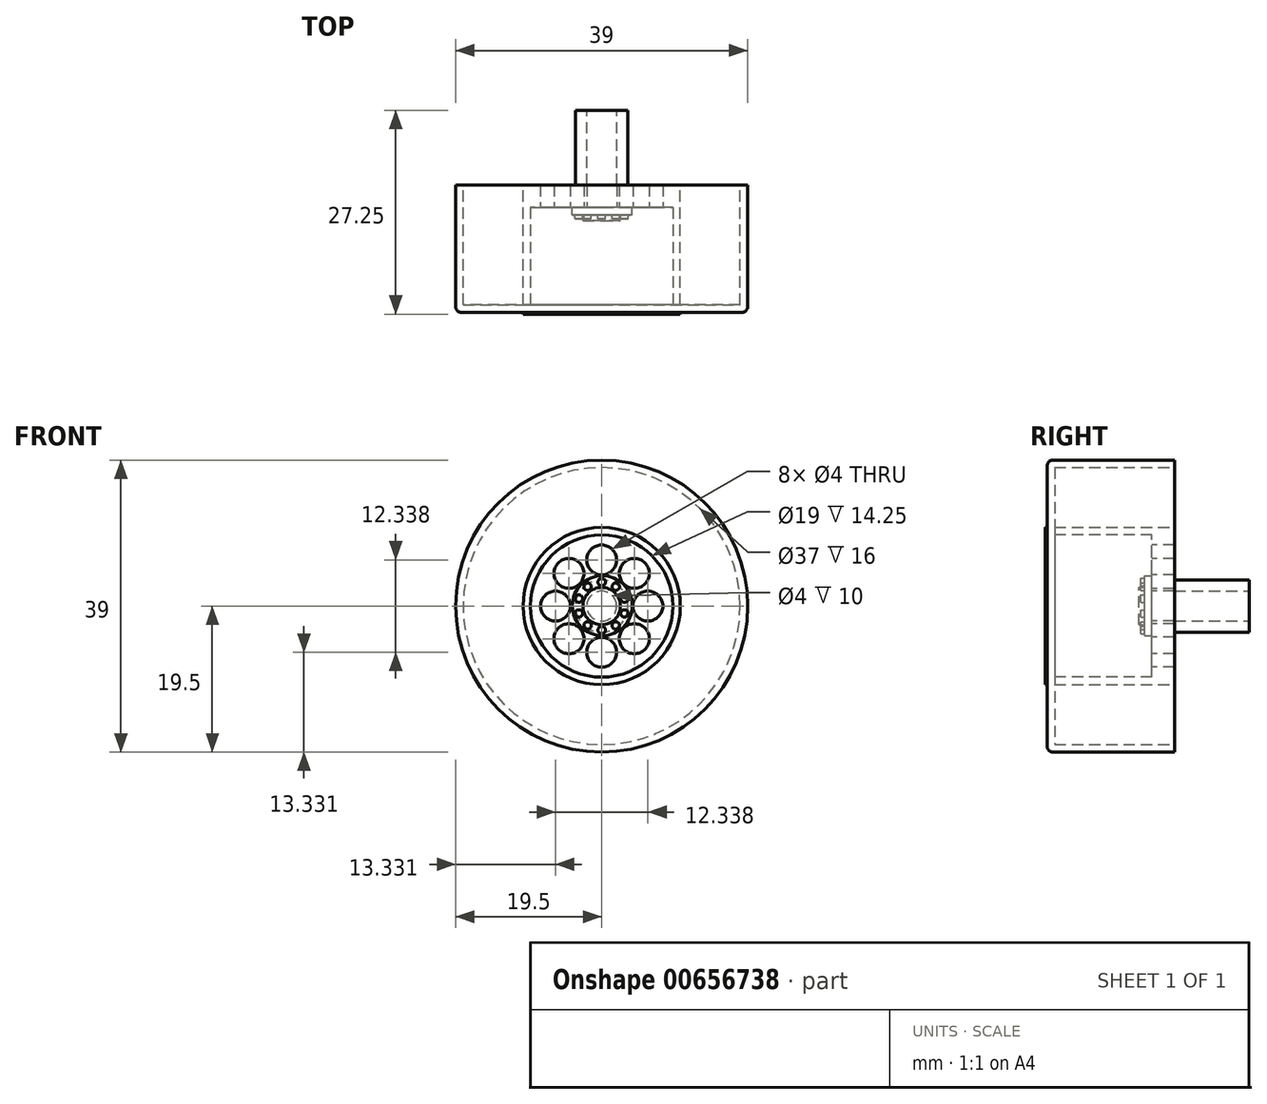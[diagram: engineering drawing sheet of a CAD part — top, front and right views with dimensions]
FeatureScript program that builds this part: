
annotation { "Feature Type Name" : "Feature", "Feature Type Description" : "" }
export const myFeature = defineFeature(function(context is Context, id is Id, definition is map)
    precondition{}
    {
        {
            var Q0;
            Q0=qCreatedBy(makeId("Front.planeOp"),FACE);
            var sketch = newSketch(context, id + "F0", { "sketchPlane" : qUnion([Q0])});
            skCircle(sketch, "E0", {"center": v(0, 0) * mm, "radius": 19.5 * mm});
            skSolve(sketch);
        }
        {
            var Q0;
            Q0=makeQuery(id+"F0.imprint","IMPRINT",FACE,{"disambiguationData":[TD([[makeQuery(id+"F0.imprint","IMPRINT",EDGE,{"derivedFrom":sQuery(id+"F0.wireOp",EDGE,"E0")}),1.0]])]});
            extrude(context, id + "F1", {"entities" : qUnion([Q0]), "depth" : 17 * mm, "offsetDistance" : 25 * mm});
        }
        {
            var Q0;
            Q0=makeQuery(id+"F1.opExtrude","CAP_FACE",FACE,{"disambiguationData":[OSD([sQuery(id+"F0.wireOp",EDGE,"E0")])],"isStart":false});
            var sketch = newSketch(context, id + "F2", { "sketchPlane" : qUnion([Q0])});
            skCircle(sketch, "E1", {"center": v(0, 0) * mm, "radius": 9.5 * mm});
            skSolve(sketch);
        }
        {
            var Q0;
            Q0=makeQuery(id+"F2.imprint","IMPRINT",FACE,{"disambiguationData":[TD([[makeQuery(id+"F2.imprint","IMPRINT",EDGE,{"derivedFrom":sQuery(id+"F2.wireOp",EDGE,"E1")}),1.0]])]});
            extrude(context, id + "F3", {"entities" : qUnion([Q0]), "operationType" : NewBodyOperationType.REMOVE, "oppositeDirection" : true, "depth" : 14 * mm, "offsetDistance" : 25 * mm});
        }
        {
            var Q0;
            Q0=makeQuery(id+"F1.opExtrude","CAP_FACE",FACE,{"disambiguationData":[OSD([sQuery(id+"F0.wireOp",EDGE,"E0")])],"isStart":true});
            var sketch = newSketch(context, id + "F4", { "sketchPlane" : qUnion([Q0])});
            skCircle(sketch, "E2", {"center": v(0, 0) * mm, "radius": 10.5 * mm});
            skCircle(sketch, "E3", {"center": v(0, 0) * mm, "radius": 18.5 * mm});
            skSolve(sketch);
        }
        {
            var Q0;
            Q0=makeQuery(id+"F4.imprint","IMPRINT",FACE,{"disambiguationData":[TD([[makeQuery(id+"F4.imprint","IMPRINT",EDGE,{"derivedFrom":sQuery(id+"F4.wireOp",EDGE,"E2")}),-1.0]])]});
            extrude(context, id + "F5", {"entities" : qUnion([Q0]), "operationType" : NewBodyOperationType.REMOVE, "oppositeDirection" : true, "depth" : 16 * mm, "offsetDistance" : 25 * mm});
        }
        {
            var Q0;
            Q0=makeQuery(id+"F3.boolean.opBoolean","COPY",FACE,{"derivedFrom":makeQuery(id+"F3.opExtrude","CAP_FACE",FACE,{"disambiguationData":[OSD([sQuery(id+"F2.wireOp",EDGE,"E1")])],"isStart":false})});
            var sketch = newSketch(context, id + "F6", { "sketchPlane" : qUnion([Q0])});
            skCircle(sketch, "E4", {"center": v(0, 6.17) * mm, "radius": 2 * mm});
            skCircle(sketch, "E5.1.0", {"center": v(-4.36, 4.36) * mm, "radius": 2 * mm});
            skCircle(sketch, "E5.2.0", {"center": v(-6.17, 0) * mm, "radius": 2 * mm});
            skCircle(sketch, "E5.3.0", {"center": v(-4.36, -4.36) * mm, "radius": 2 * mm});
            skCircle(sketch, "E5.4.0", {"center": v(0, -6.17) * mm, "radius": 2 * mm});
            skCircle(sketch, "E5.5.0", {"center": v(4.36, -4.36) * mm, "radius": 2 * mm});
            skCircle(sketch, "E5.6.0", {"center": v(6.17, 0) * mm, "radius": 2 * mm});
            skCircle(sketch, "E5.7.0", {"center": v(4.36, 4.36) * mm, "radius": 2 * mm});
            skPoint(sketch, "E5.center", {"position": v(0, 0) * mm});
            skCircle(sketch, "E6", {"center": v(0, 0) * mm, "radius": 4 * mm});
            skCircle(sketch, "E7", {"center": v(0, 0) * mm, "radius": 2.5 * mm});
            skCircle(sketch, "E8", {"center": v(0, 3.18) * mm, "radius": 0.5 * mm});
            skCircle(sketch, "E9.1.0", {"center": v(-1.87, 2.57) * mm, "radius": 0.5 * mm});
            skCircle(sketch, "E9.2.0", {"center": v(-3.02, 0.98) * mm, "radius": 0.5 * mm});
            skCircle(sketch, "E9.3.0", {"center": v(-3.02, -0.98) * mm, "radius": 0.5 * mm});
            skCircle(sketch, "E9.4.0", {"center": v(-1.87, -2.57) * mm, "radius": 0.5 * mm});
            skCircle(sketch, "E9.5.0", {"center": v(0, -3.18) * mm, "radius": 0.5 * mm});
            skCircle(sketch, "E9.6.0", {"center": v(1.87, -2.57) * mm, "radius": 0.5 * mm});
            skCircle(sketch, "E9.7.0", {"center": v(3.02, -0.98) * mm, "radius": 0.5 * mm});
            skCircle(sketch, "E9.8.0", {"center": v(3.02, 0.98) * mm, "radius": 0.5 * mm});
            skCircle(sketch, "E9.9.0", {"center": v(1.87, 2.57) * mm, "radius": 0.5 * mm});
            skSolve(sketch);
        }
        {
            var Q0;
            Q0=makeQuery(id+"F6.imprint","IMPRINT",FACE,{"disambiguationData":[TD([[makeQuery(id+"F6.imprint","IMPRINT",EDGE,{"derivedFrom":sQuery(id+"F6.wireOp",EDGE,"E4")}),1.0]])]});
            var Q1;
            Q1=makeQuery(id+"F6.imprint","IMPRINT",FACE,{"disambiguationData":[TD([[makeQuery(id+"F6.imprint","IMPRINT",EDGE,{"derivedFrom":sQuery(id+"F6.wireOp",EDGE,"E5.1.0")}),1.0]])]});
            var Q2;
            Q2=makeQuery(id+"F6.imprint","IMPRINT",FACE,{"disambiguationData":[TD([[makeQuery(id+"F6.imprint","IMPRINT",EDGE,{"derivedFrom":sQuery(id+"F6.wireOp",EDGE,"E5.2.0")}),1.0]])]});
            var Q3;
            Q3=makeQuery(id+"F6.imprint","IMPRINT",FACE,{"disambiguationData":[TD([[makeQuery(id+"F6.imprint","IMPRINT",EDGE,{"derivedFrom":sQuery(id+"F6.wireOp",EDGE,"E5.3.0")}),1.0]])]});
            var Q4;
            Q4=makeQuery(id+"F6.imprint","IMPRINT",FACE,{"disambiguationData":[TD([[makeQuery(id+"F6.imprint","IMPRINT",EDGE,{"derivedFrom":sQuery(id+"F6.wireOp",EDGE,"E5.4.0")}),1.0]])]});
            var Q5;
            Q5=makeQuery(id+"F6.imprint","IMPRINT",FACE,{"disambiguationData":[TD([[makeQuery(id+"F6.imprint","IMPRINT",EDGE,{"derivedFrom":sQuery(id+"F6.wireOp",EDGE,"E5.5.0")}),1.0]])]});
            var Q6;
            Q6=makeQuery(id+"F6.imprint","IMPRINT",FACE,{"disambiguationData":[TD([[makeQuery(id+"F6.imprint","IMPRINT",EDGE,{"derivedFrom":sQuery(id+"F6.wireOp",EDGE,"E5.6.0")}),1.0]])]});
            var Q7;
            Q7=makeQuery(id+"F6.imprint","IMPRINT",FACE,{"disambiguationData":[TD([[makeQuery(id+"F6.imprint","IMPRINT",EDGE,{"derivedFrom":sQuery(id+"F6.wireOp",EDGE,"E5.7.0")}),1.0]])]});
            extrude(context, id + "F7", {"entities" : qUnion([Q0, Q1, Q2, Q3, Q4, Q5, Q6, Q7]), "operationType" : NewBodyOperationType.REMOVE, "oppositeDirection" : true, "depth" : 25 * mm, "offsetDistance" : 25 * mm});
        }
        {
            var Q0;
            Q0=makeQuery(id+"F5.boolean.opBoolean","SPLIT",FACE,{"disambiguationData":[TD([makeQuery(id+"F5.opExtrude","SWEPT_FACE",FACE,{"disambiguationData":[OSD([sQuery(id+"F4.wireOp",EDGE,"E2")])]})])],"derivedFrom":makeQuery(id+"F1.opExtrude","CAP_FACE",FACE,{"disambiguationData":[OSD([sQuery(id+"F0.wireOp",EDGE,"E0")])],"isStart":true})});
            var sketch = newSketch(context, id + "F8", { "sketchPlane" : qUnion([Q0])});
            skCircle(sketch, "E10", {"center": v(0, 0) * mm, "radius": 3.5 * mm});
            skSolve(sketch);
        }
        {
            var Q0;
            Q0=makeQuery(id+"F8.imprint","IMPRINT",FACE,{"disambiguationData":[TD([[makeQuery(id+"F8.imprint","IMPRINT",EDGE,{"derivedFrom":sQuery(id+"F8.wireOp",EDGE,"E10")}),1.0]])]});
            extrude(context, id + "F9", {"entities" : qUnion([Q0]), "operationType" : NewBodyOperationType.ADD, "depth" : 10 * mm, "offsetDistance" : 25 * mm});
        }
        {
            var Q0;
            Q0=makeQuery(id+"F9.opExtrude","CAP_FACE",FACE,{"disambiguationData":[OSD([sQuery(id+"F8.wireOp",EDGE,"E10")])],"isStart":false});
            var sketch = newSketch(context, id + "F10", { "sketchPlane" : qUnion([Q0])});
            skCircle(sketch, "E11", {"center": v(0, 0) * mm, "radius": 2 * mm});
            skSolve(sketch);
        }
        {
            var Q0;
            Q0=makeQuery(id+"F10.imprint","IMPRINT",FACE,{"disambiguationData":[TD([[makeQuery(id+"F10.imprint","IMPRINT",EDGE,{"derivedFrom":sQuery(id+"F10.wireOp",EDGE,"E11")}),1.0]])]});
            extrude(context, id + "F11", {"entities" : qUnion([Q0]), "operationType" : NewBodyOperationType.REMOVE, "oppositeDirection" : true, "depth" : 10 * mm, "offsetDistance" : 25 * mm});
        }
        {
            var Q0;
            Q0=makeQuery(id+"F3.boolean.opBoolean","COPY",FACE,{"derivedFrom":makeQuery(id+"F3.opExtrude","CAP_FACE",FACE,{"disambiguationData":[OSD([sQuery(id+"F2.wireOp",EDGE,"E1")])],"isStart":false})});
            var sketch = newSketch(context, id + "F12", { "sketchPlane" : qUnion([Q0])});
            skCircle(sketch, "E12", {"center": v(0.09, 0.05) * mm, "radius": 4 * mm});
            skSolve(sketch);
        }
        {
            var Q0;
            Q0=makeQuery(id+"F12.imprint","IMPRINT",FACE,{"disambiguationData":[TD([[makeQuery(id+"F12.imprint","IMPRINT",EDGE,{"derivedFrom":sQuery(id+"F12.wireOp",EDGE,"E12")}),1.0]])]});
            extrude(context, id + "F13", {"entities" : qUnion([Q0]), "operationType" : NewBodyOperationType.ADD, "depth" : 1 * mm, "offsetDistance" : 25 * mm});
        }
        {
            var Q0;
            Q0=makeQuery(id+"F13.opExtrude","CAP_FACE",FACE,{"disambiguationData":[OSD([sQuery(id+"F12.wireOp",EDGE,"E12")])],"isStart":false});
            var sketch = newSketch(context, id + "F14", { "sketchPlane" : qUnion([Q0])});
            skCircle(sketch, "E13", {"center": v(0, 0) * mm, "radius": 2.5 * mm});
            skSolve(sketch);
        }
        {
            var Q0;
            Q0=makeQuery(id+"F14.imprint","IMPRINT",FACE,{"disambiguationData":[TD([[makeQuery(id+"F14.imprint","IMPRINT",EDGE,{"derivedFrom":sQuery(id+"F14.wireOp",EDGE,"E13")}),1.0]])]});
            extrude(context, id + "F15", {"entities" : qUnion([Q0]), "operationType" : NewBodyOperationType.ADD, "depth" : .75 * mm, "offsetDistance" : 25 * mm});
        }
        {
            var Q0;
            Q0=makeQuery(id+"F13.opExtrude","CAP_FACE",FACE,{"disambiguationData":[OSD([sQuery(id+"F12.wireOp",EDGE,"E12")])],"isStart":false});
            var sketch = newSketch(context, id + "F16", { "sketchPlane" : qUnion([Q0])});
            skCircle(sketch, "E14", {"center": v(0, 3.2) * mm, "radius": 0.5 * mm});
            skCircle(sketch, "E15.1.0", {"center": v(-1.89, 2.6) * mm, "radius": 0.5 * mm});
            skCircle(sketch, "E15.2.0", {"center": v(-3.05, 1) * mm, "radius": 0.5 * mm});
            skCircle(sketch, "E15.3.0", {"center": v(-3.05, -1) * mm, "radius": 0.5 * mm});
            skCircle(sketch, "E15.4.0", {"center": v(-1.89, -2.6) * mm, "radius": 0.5 * mm});
            skCircle(sketch, "E15.5.0", {"center": v(0, -3.2) * mm, "radius": 0.5 * mm});
            skCircle(sketch, "E15.6.0", {"center": v(1.89, -2.6) * mm, "radius": 0.5 * mm});
            skCircle(sketch, "E15.7.0", {"center": v(3.05, -1) * mm, "radius": 0.5 * mm});
            skCircle(sketch, "E15.8.0", {"center": v(3.05, 1) * mm, "radius": 0.5 * mm});
            skCircle(sketch, "E15.9.0", {"center": v(1.89, 2.6) * mm, "radius": 0.5 * mm});
            skPoint(sketch, "E15.center", {"position": v(0, 0) * mm});
            skSolve(sketch);
        }
        {
            var Q0;
            Q0=makeQuery(id+"F16.imprint","IMPRINT",FACE,{"disambiguationData":[TD([[makeQuery(id+"F16.imprint","IMPRINT",EDGE,{"derivedFrom":sQuery(id+"F16.wireOp",EDGE,"E14")}),1.0]])]});
            var Q1;
            Q1=makeQuery(id+"F16.imprint","IMPRINT",FACE,{"disambiguationData":[TD([[makeQuery(id+"F16.imprint","IMPRINT",EDGE,{"derivedFrom":sQuery(id+"F16.wireOp",EDGE,"E15.1.0")}),1.0]])]});
            var Q2;
            Q2=makeQuery(id+"F16.imprint","IMPRINT",FACE,{"disambiguationData":[TD([[makeQuery(id+"F16.imprint","IMPRINT",EDGE,{"derivedFrom":sQuery(id+"F16.wireOp",EDGE,"E15.2.0")}),1.0]])]});
            var Q3;
            Q3=makeQuery(id+"F16.imprint","IMPRINT",FACE,{"disambiguationData":[TD([[makeQuery(id+"F16.imprint","IMPRINT",EDGE,{"derivedFrom":sQuery(id+"F16.wireOp",EDGE,"E15.3.0")}),1.0]])]});
            var Q4;
            Q4=makeQuery(id+"F16.imprint","IMPRINT",FACE,{"disambiguationData":[TD([[makeQuery(id+"F16.imprint","IMPRINT",EDGE,{"derivedFrom":sQuery(id+"F16.wireOp",EDGE,"E15.4.0")}),1.0]])]});
            var Q5;
            Q5=makeQuery(id+"F16.imprint","IMPRINT",FACE,{"disambiguationData":[TD([[makeQuery(id+"F16.imprint","IMPRINT",EDGE,{"derivedFrom":sQuery(id+"F16.wireOp",EDGE,"E15.5.0")}),1.0]])]});
            var Q6;
            Q6=makeQuery(id+"F16.imprint","IMPRINT",FACE,{"disambiguationData":[TD([[makeQuery(id+"F16.imprint","IMPRINT",EDGE,{"derivedFrom":sQuery(id+"F16.wireOp",EDGE,"E15.6.0")}),1.0]])]});
            var Q7;
            Q7=makeQuery(id+"F16.imprint","IMPRINT",FACE,{"disambiguationData":[TD([[makeQuery(id+"F16.imprint","IMPRINT",EDGE,{"derivedFrom":sQuery(id+"F16.wireOp",EDGE,"E15.7.0")}),1.0]])]});
            var Q8;
            Q8=makeQuery(id+"F16.imprint","IMPRINT",FACE,{"disambiguationData":[TD([[makeQuery(id+"F16.imprint","IMPRINT",EDGE,{"derivedFrom":sQuery(id+"F16.wireOp",EDGE,"E15.8.0")}),1.0]])]});
            var Q9;
            Q9=makeQuery(id+"F16.imprint","IMPRINT",FACE,{"disambiguationData":[TD([[makeQuery(id+"F16.imprint","IMPRINT",EDGE,{"derivedFrom":sQuery(id+"F16.wireOp",EDGE,"E15.9.0")}),1.0]])]});
            extrude(context, id + "F17", {"entities" : qUnion([Q0, Q1, Q2, Q3, Q4, Q5, Q6, Q7, Q8, Q9]), "operationType" : NewBodyOperationType.ADD, "depth" : .5 * mm, "offsetDistance" : 25 * mm});
        }
        {
            var Q0;
            Q0=makeQuery(id+"F1.opExtrude","CAP_FACE",FACE,{"disambiguationData":[OSD([sQuery(id+"F0.wireOp",EDGE,"E0")])],"isStart":false});
            var sketch = newSketch(context, id + "F18", { "sketchPlane" : qUnion([Q0])});
            skCircle(sketch, "E16", {"center": v(0, 0) * mm, "radius": 10.5 * mm});
            skSolve(sketch);
        }
        {
            var Q0;
            Q0=makeQuery(id+"F1.opExtrude","CAP_EDGE",EDGE,{"disambiguationData":[OSD([sQuery(id+"F0.wireOp",EDGE,"E0")])],"isStart":false});
            fillet(context, id + "F19", {"entities" : qUnion([Q0]), "radius" : .75 * mm, "tangentPropagation" : true, "allowEdgeOverflow" : false});
        }
        {
            var Q0;
            Q0=makeQuery(id+"F18.imprint","IMPRINT",FACE,{"disambiguationData":[TD([[makeQuery(id+"F18.imprint","IMPRINT",EDGE,{"derivedFrom":sQuery(id+"F18.wireOp",EDGE,"E16")}),1.0]])]});
            extrude(context, id + "F20", {"entities" : qUnion([Q0]), "operationType" : NewBodyOperationType.ADD, "depth" : .25 * mm, "offsetDistance" : 25 * mm});
        }
    });
